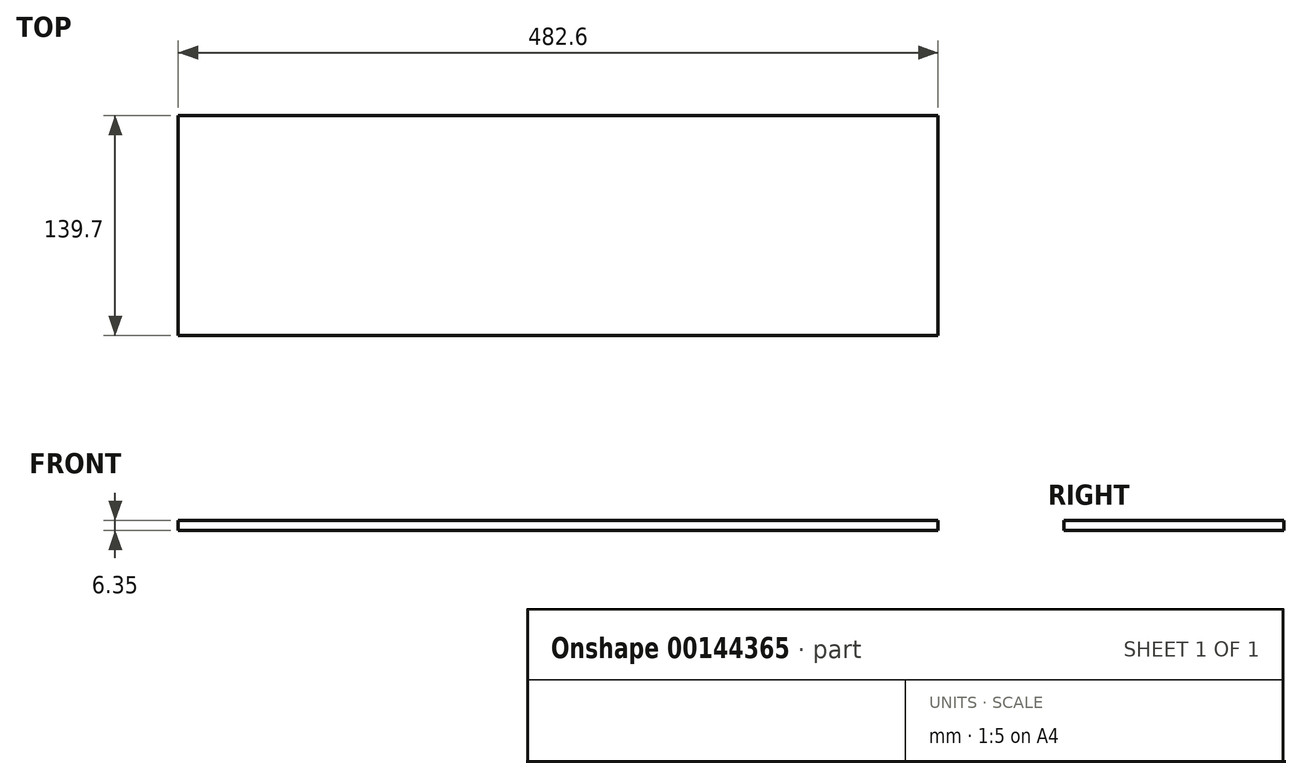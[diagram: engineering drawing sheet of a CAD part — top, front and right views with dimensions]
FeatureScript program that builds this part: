
annotation { "Feature Type Name" : "Feature", "Feature Type Description" : "" }
export const myFeature = defineFeature(function(context is Context, id is Id, definition is map)
    precondition{}
    {
        {
            var Q0;
            Q0=qCreatedBy(makeId("Top.planeOp"),FACE);
            var sketch = newSketch(context, id + "F0", { "sketchPlane" : qUnion([Q0])});
            skLineSegment(sketch, "E0.bottom", {"start": v(0, 0) * mm, "end": v(482.6, 0) * mm});
            skLineSegment(sketch, "E0.top", {"start": v(0, 139.7) * mm, "end": v(482.6, 139.7) * mm});
            skLineSegment(sketch, "E0.left", {"start": v(0, 0) * mm, "end": v(0, 139.7) * mm});
            skLineSegment(sketch, "E0.right", {"start": v(482.6, 0) * mm, "end": v(482.6, 139.7) * mm});
            skSolve(sketch);
        }
        {
            var Q0;
            Q0=makeQuery(id+"F0.imprint","IMPRINT",FACE,{"disambiguationData":[TD([[makeQuery(id+"F0.imprint","IMPRINT",EDGE,{"derivedFrom":sQuery(id+"F0.wireOp",EDGE,"E0.bottom")}),1.0]])]});
            extrude(context, id + "F1", {"entities" : qUnion([Q0]), "depth" : 6.35 * mm});
        }
    });
